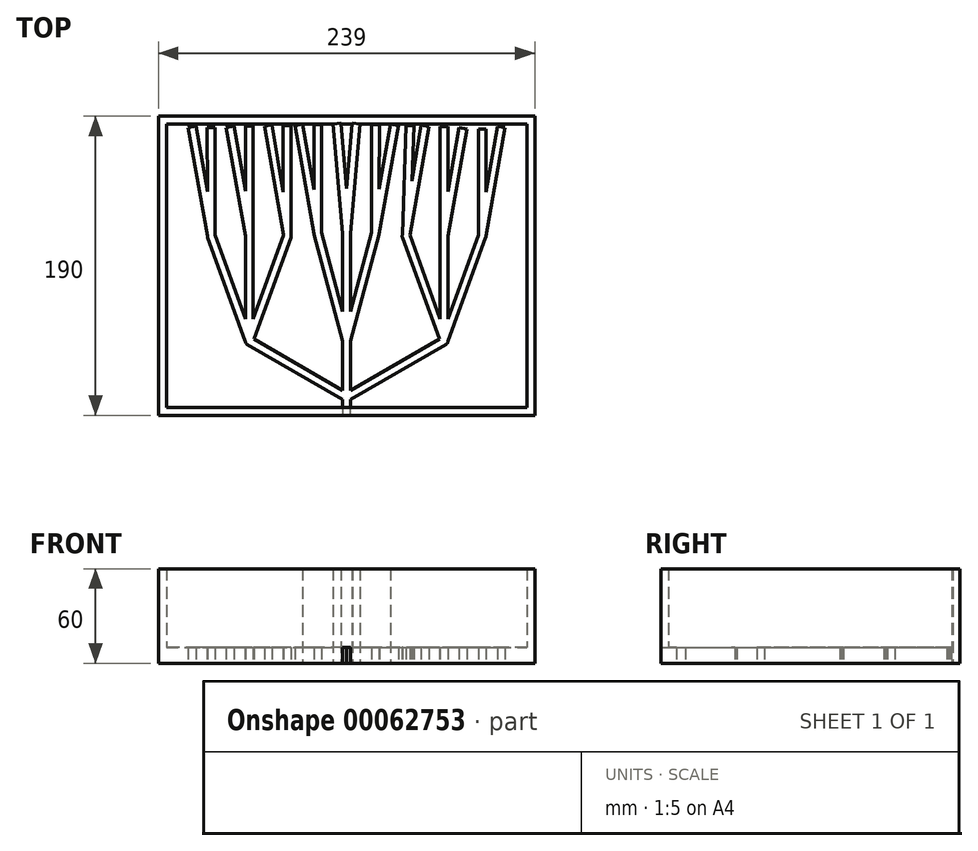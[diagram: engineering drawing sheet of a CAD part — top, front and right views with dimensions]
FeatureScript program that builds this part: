
annotation { "Feature Type Name" : "Feature", "Feature Type Description" : "" }
export const myFeature = defineFeature(function(context is Context, id is Id, definition is map)
    precondition{}
    {
        {
            var Q0;
            Q0=qCreatedBy(makeId("Top.planeOp"),FACE);
            var sketch = newSketch(context, id + "F0", { "sketchPlane" : qUnion([Q0])});
            skLineSegment(sketch, "E0", {"start": v(0, -654.78) * mm, "end": v(25, -654.78) * mm});
            skLineSegment(sketch, "E1", {"start": v(25, -672.12) * mm, "end": v(-25.43, -672.12) * mm});
            skLineSegment(sketch, "E2", {"start": v(25.6, -66.6) * mm, "end": v(20.6, -66.6) * mm});
            skLineSegment(sketch, "E3", {"start": v(20.6, -66.6) * mm, "end": v(-40.02, -31.6) * mm});
            skLineSegment(sketch, "E4", {"start": v(25.6, -66.6) * mm, "end": v(86.22, -31.6) * mm});
            skLineSegment(sketch, "E5", {"start": v(-40.02, -31.6) * mm, "end": v(-38.77, -29.43) * mm});
            skCircle(sketch, "E6", {"center": v(-38.77, -29.43) * mm, "radius": 2.5 * mm});
            skLineSegment(sketch, "E7", {"start": v(-38.77, -29.43) * mm, "end": v(-37.52, -27.27) * mm});
            skLineSegment(sketch, "E8", {"start": v(23.1, -66.6) * mm, "end": v(23.1, -64.1) * mm});
            skCircle(sketch, "E9", {"center": v(23.1, -64.1) * mm, "radius": 2.5 * mm});
            skLineSegment(sketch, "E10", {"start": v(20.6, -66.6) * mm, "end": v(23.1, -62.27) * mm});
            skLineSegment(sketch, "E11", {"start": v(23.1, -62.27) * mm, "end": v(-37.52, -27.27) * mm});
            skLineSegment(sketch, "E12", {"start": v(23.1, -62.27) * mm, "end": v(25.6, -66.6) * mm});
            skLineSegment(sketch, "E13", {"start": v(23.1, -62.27) * mm, "end": v(83.72, -27.27) * mm});
            skLineSegment(sketch, "E14", {"start": v(83.72, -27.27) * mm, "end": v(84.97, -29.43) * mm});
            skCircle(sketch, "E15", {"center": v(84.97, -29.43) * mm, "radius": 2.5 * mm});
            skLineSegment(sketch, "E16", {"start": v(-38.77, -29.43) * mm, "end": v(23.1, -29.43) * mm});
            skPoint(sketch, "E16.endSnap0", {"position": v(23.1, -65.35) * mm});
            skLineSegment(sketch, "E17", {"start": v(23.1, -29.43) * mm, "end": v(25.6, -29.43) * mm});
            skCircle(sketch, "E18", {"center": v(23.1, -29.43) * mm, "radius": 2.5 * mm});
            skLineSegment(sketch, "E19", {"start": v(20.6, -66.6) * mm, "end": v(20.6, -29.43) * mm});
            skLineSegment(sketch, "E20", {"start": v(25.6, -29.43) * mm, "end": v(25.6, -66.6) * mm});
            skLineSegment(sketch, "E21", {"start": v(20.6, -29.43) * mm, "end": v(2.48, 38.18) * mm});
            skLineSegment(sketch, "E22", {"start": v(2.48, 38.18) * mm, "end": v(7.31, 39.48) * mm});
            skLineSegment(sketch, "E23", {"start": v(7.31, 39.48) * mm, "end": v(25.6, -29.43) * mm});
            skCircle(sketch, "E24", {"center": v(4.9, 38.83) * mm, "radius": 2.5 * mm});
            skLineSegment(sketch, "E25", {"start": v(20.6, 38.83) * mm, "end": v(4.9, 38.83) * mm});
            skLineSegment(sketch, "E26", {"start": v(20.6, -29.43) * mm, "end": v(20.6, 38.83) * mm});
            skLineSegment(sketch, "E27", {"start": v(25.6, -29.43) * mm, "end": v(25.6, 38.83) * mm});
            skLineSegment(sketch, "E28", {"start": v(25.6, 38.83) * mm, "end": v(20.6, 38.83) * mm});
            skCircle(sketch, "E29", {"center": v(23.1, 38.83) * mm, "radius": 2.5 * mm});
            skLineSegment(sketch, "E30", {"start": v(25.6, -29.43) * mm, "end": v(43.72, 38.18) * mm});
            skLineSegment(sketch, "E31", {"start": v(43.72, 38.18) * mm, "end": v(38.89, 39.48) * mm});
            skLineSegment(sketch, "E32", {"start": v(38.89, 39.48) * mm, "end": v(20.6, -29.43) * mm});
            skCircle(sketch, "E33", {"center": v(41.3, 38.83) * mm, "radius": 2.5 * mm});
            skCircle(sketch, "E34", {"center": v(-62.84, 37.2) * mm, "radius": 2.5 * mm});
            skLineSegment(sketch, "E35", {"start": v(-41.25, -29.43) * mm, "end": v(-65.19, 36.35) * mm});
            skLineSegment(sketch, "E36", {"start": v(-60.49, 38.06) * mm, "end": v(-36.25, -29.43) * mm});
            skLineSegment(sketch, "E37", {"start": v(-41.25, 37.2) * mm, "end": v(-62.84, 37.2) * mm});
            skCircle(sketch, "E38", {"center": v(-38.75, 37.2) * mm, "radius": 2.5 * mm});
            skLineSegment(sketch, "E39", {"start": v(-36.25, -29.43) * mm, "end": v(-12.3, 36.35) * mm});
            skLineSegment(sketch, "E40", {"start": v(-17, 38.06) * mm, "end": v(-12.3, 36.35) * mm});
            skCircle(sketch, "E41", {"center": v(-14.65, 37.2) * mm, "radius": 2.5 * mm});
            skLineSegment(sketch, "E42", {"start": v(-36.25, -29.43) * mm, "end": v(-36.25, 37.2) * mm});
            skLineSegment(sketch, "E43", {"start": v(-41.25, 37.2) * mm, "end": v(-41.25, -29.43) * mm});
            skCircle(sketch, "E44", {"center": v(60.88, 37.14) * mm, "radius": 2.5 * mm});
            skLineSegment(sketch, "E45", {"start": v(82.47, -29.49) * mm, "end": v(58.53, 36.29) * mm});
            skLineSegment(sketch, "E46", {"start": v(63.23, 38) * mm, "end": v(87.47, -29.49) * mm});
            skLineSegment(sketch, "E47", {"start": v(82.47, 37.14) * mm, "end": v(60.88, 37.14) * mm});
            skCircle(sketch, "E48", {"center": v(84.97, 37.14) * mm, "radius": 2.5 * mm});
            skLineSegment(sketch, "E49", {"start": v(106.72, 38) * mm, "end": v(82.47, -29.49) * mm});
            skLineSegment(sketch, "E50", {"start": v(87.47, -29.49) * mm, "end": v(111.41, 36.29) * mm});
            skLineSegment(sketch, "E51", {"start": v(106.72, 38) * mm, "end": v(111.41, 36.29) * mm});
            skCircle(sketch, "E52", {"center": v(109.06, 37.14) * mm, "radius": 2.5 * mm});
            skLineSegment(sketch, "E53", {"start": v(87.47, -29.49) * mm, "end": v(87.47, 37.14) * mm});
            skLineSegment(sketch, "E54", {"start": v(82.47, 37.14) * mm, "end": v(82.47, -29.49) * mm});
            skLineSegment(sketch, "E55", {"start": v(-17, 38.06) * mm, "end": v(-41.25, -29.43) * mm});
            skLineSegment(sketch, "E56", {"start": v(20.6, 38.83) * mm, "end": v(14.5, 108.56) * mm});
            skLineSegment(sketch, "E57", {"start": v(25.6, 38.83) * mm, "end": v(31.7, 108.56) * mm});
            skLineSegment(sketch, "E58", {"start": v(14.5, 108.56) * mm, "end": v(19.48, 109) * mm});
            skLineSegment(sketch, "E59", {"start": v(31.7, 108.56) * mm, "end": v(26.72, 109) * mm});
            skLineSegment(sketch, "E60", {"start": v(26.72, 109) * mm, "end": v(20.6, 38.83) * mm});
            skLineSegment(sketch, "E61", {"start": v(19.48, 109) * mm, "end": v(25.6, 38.83) * mm});
            skLineSegment(sketch, "E62", {"start": v(7.31, 39.48) * mm, "end": v(7.31, 108.09) * mm});
            skLineSegment(sketch, "E63", {"start": v(2.48, 108.09) * mm, "end": v(2.48, 38.18) * mm});
            skLineSegment(sketch, "E64", {"start": v(2.48, 108.09) * mm, "end": v(7.31, 108.09) * mm});
            skLineSegment(sketch, "E65", {"start": v(7.31, 39.48) * mm, "end": v(-4.84, 108.41) * mm});
            skLineSegment(sketch, "E66", {"start": v(-4.84, 108.41) * mm, "end": v(-9.77, 107.54) * mm});
            skLineSegment(sketch, "E67", {"start": v(-9.77, 107.54) * mm, "end": v(2.48, 38.18) * mm});
            skLineSegment(sketch, "E68", {"start": v(38.89, 39.48) * mm, "end": v(38.89, 108.09) * mm});
            skLineSegment(sketch, "E69", {"start": v(38.89, 108.09) * mm, "end": v(43.89, 108.09) * mm});
            skLineSegment(sketch, "E70", {"start": v(43.89, 108.09) * mm, "end": v(43.72, 38.18) * mm});
            skLineSegment(sketch, "E71", {"start": v(38.89, 39.48) * mm, "end": v(51.04, 108.41) * mm});
            skLineSegment(sketch, "E72", {"start": v(51.04, 108.41) * mm, "end": v(55.97, 107.54) * mm});
            skLineSegment(sketch, "E73", {"start": v(55.97, 107.54) * mm, "end": v(43.72, 38.18) * mm});
            skLineSegment(sketch, "E74", {"start": v(58.53, 36.29) * mm, "end": v(60.88, 107.54) * mm});
            skLineSegment(sketch, "E75", {"start": v(60.88, 107.54) * mm, "end": v(65.88, 107.38) * mm});
            skLineSegment(sketch, "E76", {"start": v(65.88, 107.38) * mm, "end": v(63.23, 38) * mm});
            skLineSegment(sketch, "E77", {"start": v(-12.3, 36.35) * mm, "end": v(-12.3, 107.54) * mm});
            skLineSegment(sketch, "E78", {"start": v(-12.3, 107.54) * mm, "end": v(-17.3, 107.54) * mm});
            skLineSegment(sketch, "E79", {"start": v(-17.3, 107.54) * mm, "end": v(-17, 38.06) * mm});
            skLineSegment(sketch, "E80", {"start": v(-17, 38.06) * mm, "end": v(-29.16, 107) * mm});
            skLineSegment(sketch, "E81", {"start": v(-29.16, 107) * mm, "end": v(-24.23, 107.86) * mm});
            skLineSegment(sketch, "E82", {"start": v(-24.23, 107.86) * mm, "end": v(-12.3, 36.35) * mm});
            skLineSegment(sketch, "E83", {"start": v(63.23, 38) * mm, "end": v(75.38, 106.94) * mm});
            skLineSegment(sketch, "E84", {"start": v(75.38, 106.94) * mm, "end": v(70.46, 107.8) * mm});
            skLineSegment(sketch, "E85", {"start": v(70.46, 107.8) * mm, "end": v(58.53, 36.29) * mm});
            skLineSegment(sketch, "E86", {"start": v(82.47, 37.14) * mm, "end": v(82.47, 106.94) * mm});
            skLineSegment(sketch, "E87", {"start": v(82.47, 106.94) * mm, "end": v(87.47, 106.94) * mm});
            skLineSegment(sketch, "E88", {"start": v(87.47, 106.94) * mm, "end": v(87.47, 37.14) * mm});
            skLineSegment(sketch, "E89", {"start": v(82.47, 37.14) * mm, "end": v(94.63, 106.08) * mm});
            skLineSegment(sketch, "E90", {"start": v(94.63, 106.08) * mm, "end": v(99.55, 105.21) * mm});
            skLineSegment(sketch, "E91", {"start": v(99.55, 105.21) * mm, "end": v(87.47, 37.14) * mm});
            skLineSegment(sketch, "E92", {"start": v(-36.25, 37.2) * mm, "end": v(-36.25, 107) * mm});
            skLineSegment(sketch, "E93", {"start": v(-41.25, 37.2) * mm, "end": v(-41.25, 107) * mm});
            skLineSegment(sketch, "E94", {"start": v(-41.25, 107) * mm, "end": v(-36.25, 107) * mm});
            skLineSegment(sketch, "E95", {"start": v(-41.25, 37.2) * mm, "end": v(-53.4, 106.14) * mm});
            skLineSegment(sketch, "E96", {"start": v(-53.4, 106.14) * mm, "end": v(-48.48, 107) * mm});
            skLineSegment(sketch, "E97", {"start": v(-48.48, 107) * mm, "end": v(-36.25, 37.2) * mm});
            skLineSegment(sketch, "E98", {"start": v(-60.49, 38.06) * mm, "end": v(-60.49, 106.14) * mm});
            skLineSegment(sketch, "E99", {"start": v(-60.49, 106.14) * mm, "end": v(-65.49, 106.14) * mm});
            skLineSegment(sketch, "E100", {"start": v(-65.49, 106.14) * mm, "end": v(-65.19, 36.35) * mm});
            skLineSegment(sketch, "E101", {"start": v(-60.49, 38.06) * mm, "end": v(-72.64, 107) * mm});
            skLineSegment(sketch, "E102", {"start": v(-72.64, 107) * mm, "end": v(-77.57, 106.13) * mm});
            skLineSegment(sketch, "E103", {"start": v(-77.57, 106.13) * mm, "end": v(-65.19, 36.35) * mm});
            skLineSegment(sketch, "E104", {"start": v(106.72, 38) * mm, "end": v(106.72, 105.21) * mm});
            skLineSegment(sketch, "E105", {"start": v(106.72, 105.21) * mm, "end": v(111.72, 105.21) * mm});
            skLineSegment(sketch, "E106", {"start": v(111.72, 105.21) * mm, "end": v(111.41, 36.29) * mm});
            skLineSegment(sketch, "E107", {"start": v(106.72, 38) * mm, "end": v(118.87, 106.94) * mm});
            skLineSegment(sketch, "E108", {"start": v(118.87, 106.94) * mm, "end": v(123.8, 106.07) * mm});
            skLineSegment(sketch, "E109", {"start": v(123.8, 106.07) * mm, "end": v(111.41, 36.29) * mm});
            skLineSegment(sketch, "E110", {"start": v(20.6, -66.6) * mm, "end": v(20.6, -76.6) * mm});
            skLineSegment(sketch, "E111", {"start": v(20.6, -76.6) * mm, "end": v(25.6, -76.6) * mm});
            skLineSegment(sketch, "E112", {"start": v(25.6, -76.6) * mm, "end": v(25.6, -66.6) * mm});
            skLineSegment(sketch, "E113", {"start": v(25.6, -76.6) * mm, "end": v(142.6, -76.6) * mm});
            skLineSegment(sketch, "E114", {"start": v(20.6, -76.6) * mm, "end": v(-96.4, -76.6) * mm});
            skLineSegment(sketch, "E115", {"start": v(-96.4, -76.6) * mm, "end": v(-96.4, 113.4) * mm});
            skLineSegment(sketch, "E116", {"start": v(-96.4, 113.4) * mm, "end": v(142.6, 113.4) * mm});
            skLineSegment(sketch, "E117", {"start": v(142.6, 113.4) * mm, "end": v(142.6, -76.6) * mm});
            skSolve(sketch);
        }
        {
            var Q0;
            {var subQ120=sQuery(id+"F0.wireOp",EDGE,"E3");Q0=makeQuery(id+"F0.imprint","IMPRINT",FACE,{"disambiguationData":[TD([[makeQuery(id+"F0.imprint","IMPRINT",EDGE,{"derivedFrom":subQ120}),1.0]])]});}
            var Q1;
            {var subQ0=sQuery(id+"F0.wireOp",EDGE,"E19");var subQ1=sQuery(id+"F0.wireOp",EDGE,"E11");var subQ2=makeQuery(id+"F0.imprint","INTERSECT",VERTEX,{"derivedFrom":[subQ1,subQ0]});Q1=makeQuery(id+"F0.imprint","IMPRINT",FACE,{"disambiguationData":[TD([[makeQuery(id+"F0.imprint","IMPRINT",EDGE,{"disambiguationData":[TD([[subQ2,-1.0]])],"derivedFrom":subQ1}),-1.0]])]});}
            var Q2;
            {var subQ0=sQuery(id+"F0.wireOp",EDGE,"E37");var subQ1=sQuery(id+"F0.wireOp",EDGE,"E36");var subQ2=makeQuery(id+"F0.imprint","INTERSECT",VERTEX,{"derivedFrom":[subQ1,subQ0]});Q2=makeQuery(id+"F0.imprint","IMPRINT",FACE,{"disambiguationData":[TD([[makeQuery(id+"F0.imprint","IMPRINT",EDGE,{"disambiguationData":[TD([[subQ2,-1.0]])],"derivedFrom":subQ1}),1.0]])]});}
            var Q3;
            {var subQ0=sQuery(id+"F0.wireOp",EDGE,"E25");var subQ1=sQuery(id+"F0.wireOp",EDGE,"E23");var subQ2=makeQuery(id+"F0.imprint","INTERSECT",VERTEX,{"derivedFrom":[subQ1,subQ0]});Q3=makeQuery(id+"F0.imprint","IMPRINT",FACE,{"disambiguationData":[TD([[makeQuery(id+"F0.imprint","IMPRINT",EDGE,{"disambiguationData":[TD([[subQ2,-1.0]])],"derivedFrom":subQ1}),1.0]])]});}
            var Q4;
            {var subQ0=sQuery(id+"F0.wireOp",EDGE,"E47");var subQ1=sQuery(id+"F0.wireOp",EDGE,"E46");var subQ2=makeQuery(id+"F0.imprint","INTERSECT",VERTEX,{"derivedFrom":[subQ1,subQ0]});Q4=makeQuery(id+"F0.imprint","IMPRINT",FACE,{"disambiguationData":[TD([[makeQuery(id+"F0.imprint","IMPRINT",EDGE,{"disambiguationData":[TD([[subQ2,-1.0]])],"derivedFrom":subQ1}),1.0]])]});}
            extrude(context, id + "F1", {"entities" : qUnion([Q0, Q1, Q2, Q3, Q4]), "depth" : 10 * mm});
        }
        {
            var Q0;
            Q0=makeQuery(id+"F1.opExtrude","CAP_FACE",FACE,{"disambiguationData":[OSD([sQuery(id+"F0.wireOp",EDGE,"E3"),sQuery(id+"F0.wireOp",EDGE,"E4"),sQuery(id+"F0.wireOp",EDGE,"E6"),sQuery(id+"F0.wireOp",EDGE,"E11"),sQuery(id+"F0.wireOp",EDGE,"E13"),sQuery(id+"F0.wireOp",EDGE,"E15"),sQuery(id+"F0.wireOp",EDGE,"E19"),sQuery(id+"F0.wireOp",EDGE,"E20"),sQuery(id+"F0.wireOp",EDGE,"E21"),sQuery(id+"F0.wireOp",EDGE,"E23"),sQuery(id+"F0.wireOp",EDGE,"E24"),sQuery(id+"F0.wireOp",EDGE,"E26"),sQuery(id+"F0.wireOp",EDGE,"E27"),sQuery(id+"F0.wireOp",EDGE,"E30"),sQuery(id+"F0.wireOp",EDGE,"E32"),sQuery(id+"F0.wireOp",EDGE,"E33"),sQuery(id+"F0.wireOp",EDGE,"E34"),sQuery(id+"F0.wireOp",EDGE,"E35"),sQuery(id+"F0.wireOp",EDGE,"E36"),sQuery(id+"F0.wireOp",EDGE,"E39"),sQuery(id+"F0.wireOp",EDGE,"E41"),sQuery(id+"F0.wireOp",EDGE,"E42"),sQuery(id+"F0.wireOp",EDGE,"E43"),sQuery(id+"F0.wireOp",EDGE,"E44"),sQuery(id+"F0.wireOp",EDGE,"E45"),sQuery(id+"F0.wireOp",EDGE,"E46"),sQuery(id+"F0.wireOp",EDGE,"E49"),sQuery(id+"F0.wireOp",EDGE,"E50"),sQuery(id+"F0.wireOp",EDGE,"E52"),sQuery(id+"F0.wireOp",EDGE,"E53"),sQuery(id+"F0.wireOp",EDGE,"E54"),sQuery(id+"F0.wireOp",EDGE,"E55"),sQuery(id+"F0.wireOp",EDGE,"E56"),sQuery(id+"F0.wireOp",EDGE,"E57"),sQuery(id+"F0.wireOp",EDGE,"E58"),sQuery(id+"F0.wireOp",EDGE,"E59"),sQuery(id+"F0.wireOp",EDGE,"E60"),sQuery(id+"F0.wireOp",EDGE,"E61"),sQuery(id+"F0.wireOp",EDGE,"E62"),sQuery(id+"F0.wireOp",EDGE,"E63"),sQuery(id+"F0.wireOp",EDGE,"E64"),sQuery(id+"F0.wireOp",EDGE,"E65"),sQuery(id+"F0.wireOp",EDGE,"E66"),sQuery(id+"F0.wireOp",EDGE,"E67"),sQuery(id+"F0.wireOp",EDGE,"E68"),sQuery(id+"F0.wireOp",EDGE,"E69"),sQuery(id+"F0.wireOp",EDGE,"E70"),sQuery(id+"F0.wireOp",EDGE,"E71"),sQuery(id+"F0.wireOp",EDGE,"E72"),sQuery(id+"F0.wireOp",EDGE,"E73"),sQuery(id+"F0.wireOp",EDGE,"E74"),sQuery(id+"F0.wireOp",EDGE,"E75"),sQuery(id+"F0.wireOp",EDGE,"E76"),sQuery(id+"F0.wireOp",EDGE,"E77"),sQuery(id+"F0.wireOp",EDGE,"E78"),sQuery(id+"F0.wireOp",EDGE,"E79"),sQuery(id+"F0.wireOp",EDGE,"E80"),sQuery(id+"F0.wireOp",EDGE,"E81"),sQuery(id+"F0.wireOp",EDGE,"E82"),sQuery(id+"F0.wireOp",EDGE,"E83"),sQuery(id+"F0.wireOp",EDGE,"E84"),sQuery(id+"F0.wireOp",EDGE,"E85"),sQuery(id+"F0.wireOp",EDGE,"E86"),sQuery(id+"F0.wireOp",EDGE,"E87"),sQuery(id+"F0.wireOp",EDGE,"E88"),sQuery(id+"F0.wireOp",EDGE,"E89"),sQuery(id+"F0.wireOp",EDGE,"E90"),sQuery(id+"F0.wireOp",EDGE,"E91"),sQuery(id+"F0.wireOp",EDGE,"E92"),sQuery(id+"F0.wireOp",EDGE,"E93"),sQuery(id+"F0.wireOp",EDGE,"E94"),sQuery(id+"F0.wireOp",EDGE,"E95"),sQuery(id+"F0.wireOp",EDGE,"E96"),sQuery(id+"F0.wireOp",EDGE,"E97"),sQuery(id+"F0.wireOp",EDGE,"E98"),sQuery(id+"F0.wireOp",EDGE,"E99"),sQuery(id+"F0.wireOp",EDGE,"E100"),sQuery(id+"F0.wireOp",EDGE,"E101"),sQuery(id+"F0.wireOp",EDGE,"E102"),sQuery(id+"F0.wireOp",EDGE,"E103"),sQuery(id+"F0.wireOp",EDGE,"E104"),sQuery(id+"F0.wireOp",EDGE,"E105"),sQuery(id+"F0.wireOp",EDGE,"E106"),sQuery(id+"F0.wireOp",EDGE,"E107"),sQuery(id+"F0.wireOp",EDGE,"E108"),sQuery(id+"F0.wireOp",EDGE,"E109"),sQuery(id+"F0.wireOp",EDGE,"E110"),sQuery(id+"F0.wireOp",EDGE,"E112"),sQuery(id+"F0.wireOp",EDGE,"E113"),sQuery(id+"F0.wireOp",EDGE,"E114"),sQuery(id+"F0.wireOp",EDGE,"E115"),sQuery(id+"F0.wireOp",EDGE,"E116"),sQuery(id+"F0.wireOp",EDGE,"E117")])],"isStart":false});
            var sketch = newSketch(context, id + "F2", { "sketchPlane" : qUnion([Q0])});
            skLineSegment(sketch, "E118", {"start": v(-96.4, -76.6) * mm, "end": v(-96.4, 113.4) * mm});
            skLineSegment(sketch, "E119", {"start": v(-96.4, 113.4) * mm, "end": v(142.6, 113.4) * mm});
            skLineSegment(sketch, "E120", {"start": v(142.6, 113.4) * mm, "end": v(142.6, -76.6) * mm});
            skLineSegment(sketch, "E121", {"start": v(142.6, -76.6) * mm, "end": v(-96.4, -76.6) * mm});
            skLineSegment(sketch, "E122", {"start": v(-91.4, -76.6) * mm, "end": v(-91.4, -71.6) * mm});
            skLineSegment(sketch, "E123", {"start": v(-91.4, 113.4) * mm, "end": v(-91.4, 108.4) * mm});
            skLineSegment(sketch, "E124", {"start": v(142.6, 108.4) * mm, "end": v(137.6, 108.4) * mm});
            skLineSegment(sketch, "E125", {"start": v(142.6, -67.48) * mm, "end": v(137.6, -67.48) * mm});
            skLineSegment(sketch, "E126", {"start": v(-91.4, -71.6) * mm, "end": v(-91.4, 108.4) * mm});
            skLineSegment(sketch, "E127", {"start": v(-91.4, 108.4) * mm, "end": v(137.6, 108.4) * mm});
            skLineSegment(sketch, "E128", {"start": v(137.6, 108.4) * mm, "end": v(137.6, -71.6) * mm});
            skLineSegment(sketch, "E129", {"start": v(137.6, -71.6) * mm, "end": v(-91.4, -71.6) * mm});
            skSolve(sketch);
        }
        {
            var Q0;
            {var subQ0=sQuery(id+"F2.wireOp",EDGE,"E121");var subQ1=makeQuery(id+"F1.opExtrude","CAP_EDGE",EDGE,{"disambiguationData":[OSD([sQuery(id+"F0.wireOp",EDGE,"E110")])],"isStart":false});var subQ2=makeQuery(id+"F2.imprint","INTERSECT",VERTEX,{"derivedFrom":[subQ1,subQ0]});Q0=makeQuery(id+"F2.imprint","IMPRINT",FACE,{"disambiguationData":[TD([[makeQuery(id+"F2.imprint","IMPRINT",EDGE,{"disambiguationData":[TD([[subQ2,1.0]])],"derivedFrom":subQ0}),-1.0]])]});}
            var Q1;
            {var subQ1=sQuery(id+"F2.wireOp",EDGE,"E125");Q1=makeQuery(id+"F2.imprint","IMPRINT",FACE,{"disambiguationData":[TD([[makeQuery(id+"F2.imprint","IMPRINT",EDGE,{"derivedFrom":subQ1}),1.0]])]});}
            var Q2;
            {var subQ3=sQuery(id+"F2.wireOp",EDGE,"E122");Q2=makeQuery(id+"F2.imprint","IMPRINT",FACE,{"disambiguationData":[TD([[makeQuery(id+"F2.imprint","IMPRINT",EDGE,{"derivedFrom":subQ3}),-1.0]])]});}
            var Q3;
            {var subQ2=sQuery(id+"F2.wireOp",EDGE,"E118");Q3=makeQuery(id+"F2.imprint","IMPRINT",FACE,{"disambiguationData":[TD([[makeQuery(id+"F2.imprint","IMPRINT",EDGE,{"derivedFrom":subQ2}),-1.0]])]});}
            var Q4;
            {var subQ0=sQuery(id+"F2.wireOp",EDGE,"E124");Q4=makeQuery(id+"F2.imprint","IMPRINT",FACE,{"disambiguationData":[TD([[makeQuery(id+"F2.imprint","IMPRINT",EDGE,{"derivedFrom":subQ0}),1.0]])]});}
            var Q5;
            {var subQ16=sQuery(id+"F2.wireOp",EDGE,"E123");Q5=makeQuery(id+"F2.imprint","IMPRINT",FACE,{"disambiguationData":[TD([[makeQuery(id+"F2.imprint","IMPRINT",EDGE,{"derivedFrom":subQ16}),1.0]])]});}
            extrude(context, id + "F3", {"entities" : qUnion([Q0, Q1, Q2, Q3, Q4, Q5]), "operationType" : NewBodyOperationType.ADD, "depth" : 50 * mm});
        }
    });
